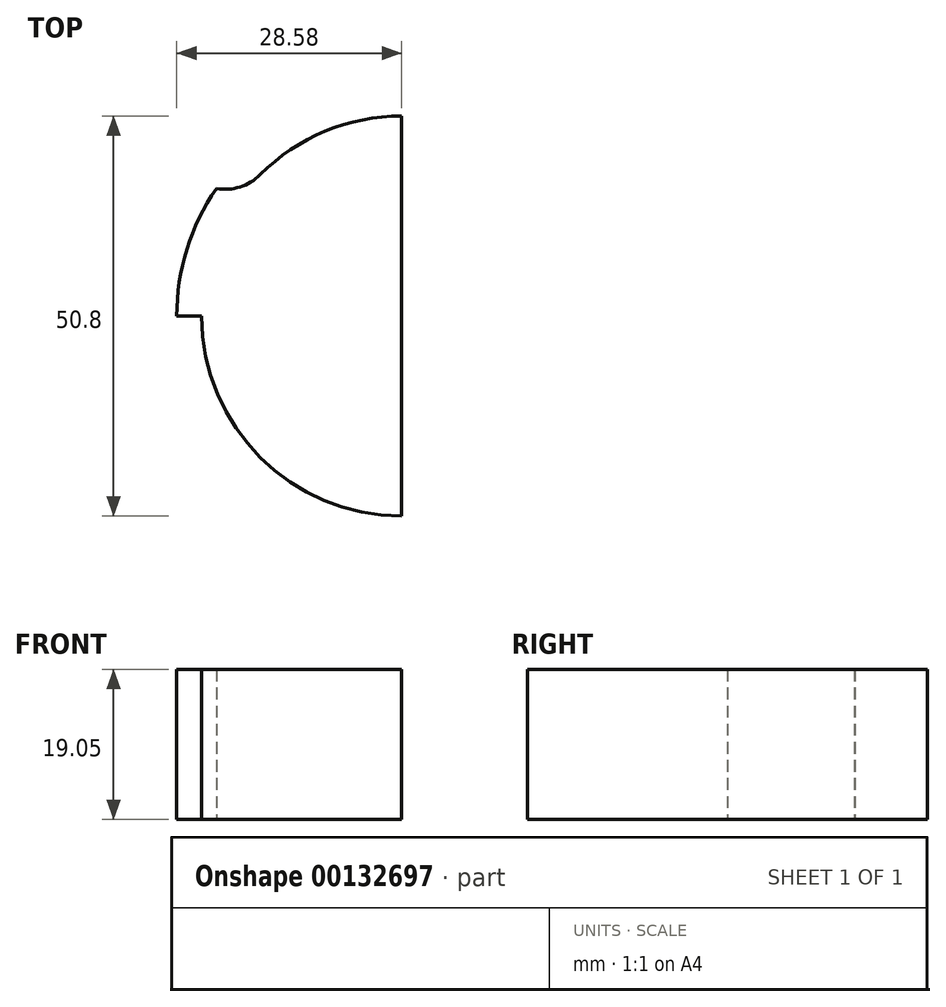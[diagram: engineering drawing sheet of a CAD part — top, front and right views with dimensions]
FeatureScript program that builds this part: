
annotation { "Feature Type Name" : "Feature", "Feature Type Description" : "" }
export const myFeature = defineFeature(function(context is Context, id is Id, definition is map)
    precondition{}
    {
        {
            var Q0;
            Q0=qCreatedBy(makeId("Top.planeOp"),FACE);
            var sketch = newSketch(context, id + "F0", { "sketchPlane" : qUnion([Q0])});
            skCircle(sketch, "E0", {"center": v(0, 0) * mm, "radius": 44.45 * mm});
            skLineSegment(sketch, "E1", {"start": v(0, 72.68) * mm, "end": v(0, -70.78) * mm});
            skLineSegment(sketch, "E2", {"start": v(70.46, 0) * mm, "end": v(38.1, 0) * mm});
            skArc(sketch, "E3", {"start": v(-34.92, 0) * mm, "mid": v(-31.75, -3.18) * mm, "end": v(-28.57, 0) * mm});
            skLineSegment(sketch, "E4.trimOffspring", {"start": v(-34.92, 0) * mm, "end": v(-64.18, 0) * mm});
            skLineSegment(sketch, "E5.trimOffspring", {"start": v(25.4, 0) * mm, "end": v(-28.57, 0) * mm});
            skArc(sketch, "E6", {"start": v(-23.54, 16.2) * mm, "mid": v(-27.29, 8.48) * mm, "end": v(-28.57, 0) * mm});
            skArc(sketch, "E7", {"start": v(-28.42, 20.3) * mm, "mid": v(-33.26, 10.66) * mm, "end": v(-34.92, 0) * mm});
            skLineSegment(sketch, "E8", {"start": v(0, 0) * mm, "end": v(-28.57, 0) * mm});
            skArc(sketch, "E9.MirrorC", {"start": v(-23.54, 16.2) * mm, "mid": v(-18.37, 27.31) * mm, "end": v(-28.42, 20.3) * mm});
            skArc(sketch, "E10.MirrorC", {"start": v(17.96, -17.96) * mm, "mid": v(17.96, -26.94) * mm, "end": v(26.94, -26.94) * mm});
            skArc(sketch, "E11", {"start": v(0, 25.4) * mm, "mid": v(-25.4, 0) * mm, "end": v(0, -25.4) * mm});
            skArc(sketch, "E12", {"start": v(0, 38.1) * mm, "mid": v(-38.1, 0) * mm, "end": v(0, -38.1) * mm});
            skArc(sketch, "E13", {"start": v(38.1, 0) * mm, "mid": v(31.75, 6.35) * mm, "end": v(25.4, 0) * mm});
            skArc(sketch, "E14.trimOffspring", {"start": v(17.96, -17.96) * mm, "mid": v(23.47, -9.72) * mm, "end": v(25.4, 0) * mm});
            skArc(sketch, "E15.trimOffspring", {"start": v(26.94, -26.94) * mm, "mid": v(35.2, -14.58) * mm, "end": v(38.1, 0) * mm});
            skSolve(sketch);
        }
        {
            var Q0;
            {var subQ0=sQuery(id+"F0.wireOp",EDGE,"E5.trimOffspring");Q0=makeQuery(id+"F0.imprint","IMPRINT",FACE,{"disambiguationData":[TD([[makeQuery(id+"F0.imprint","IMPRINT",EDGE,{"derivedFrom":subQ0}),-1.0]])]});}
            var Q1;
            {var subQ0=sQuery(id+"F0.wireOp",EDGE,"E5.trimOffspring");Q1=makeQuery(id+"F0.imprint","IMPRINT",FACE,{"disambiguationData":[TD([[makeQuery(id+"F0.imprint","IMPRINT",EDGE,{"derivedFrom":subQ0}),1.0]])]});}
            extrude(context, id + "F1", {"entities" : qUnion([Q0, Q1]), "depth" : 19.05 * mm});
        }
    });
